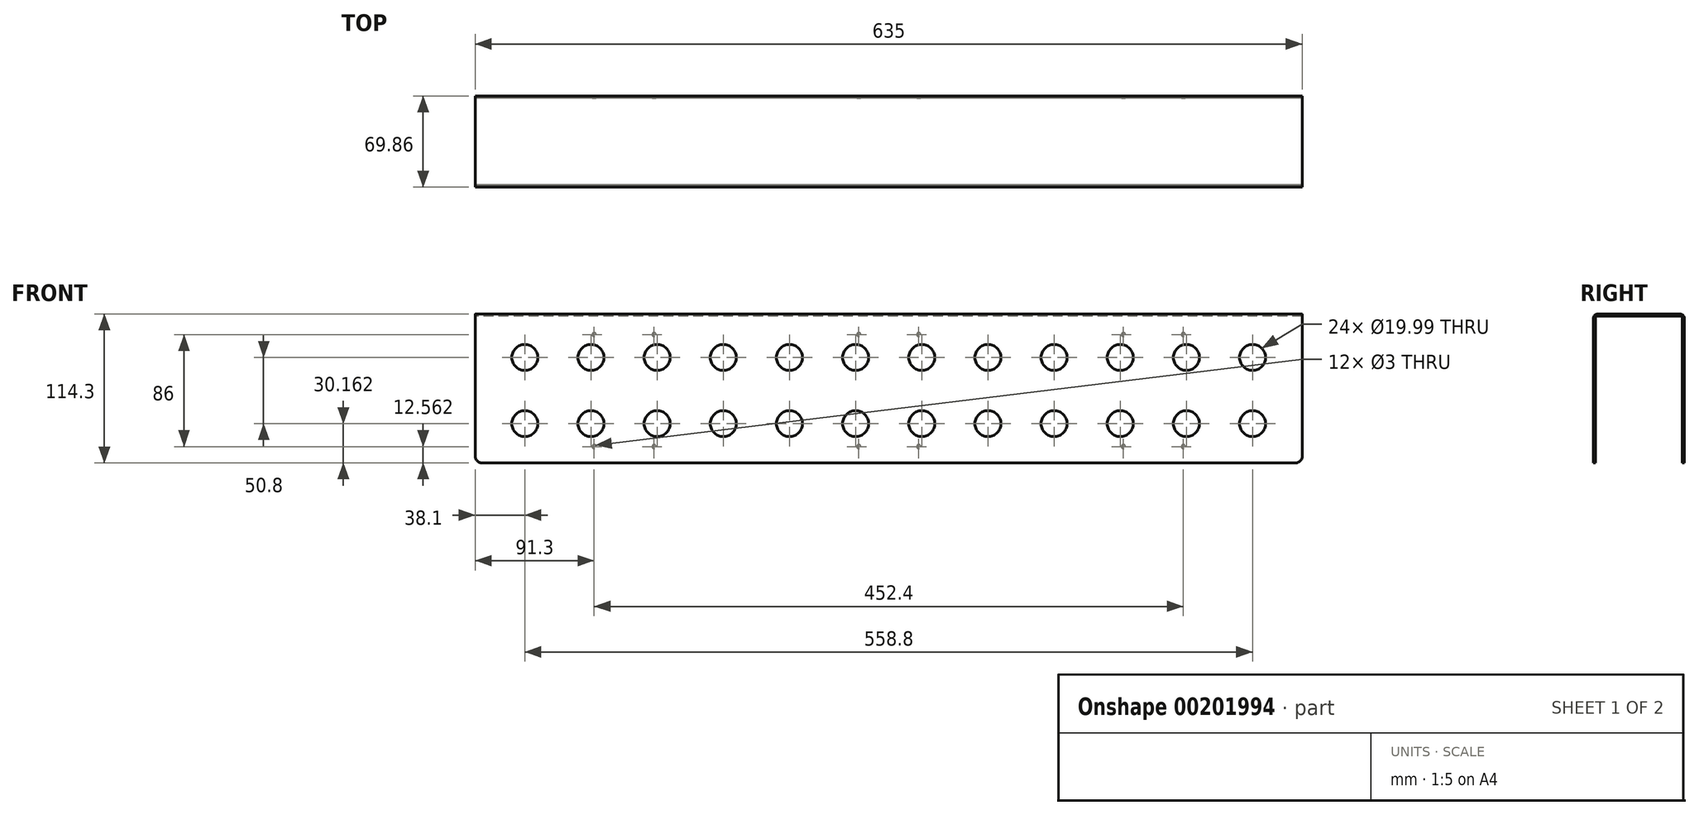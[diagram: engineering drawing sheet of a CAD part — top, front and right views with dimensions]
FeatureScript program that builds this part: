
annotation { "Feature Type Name" : "Feature", "Feature Type Description" : "" }
export const myFeature = defineFeature(function(context is Context, id is Id, definition is map)
    precondition{}
    {
        {
            var Q0;
            Q0=qCreatedBy(makeId("Right.planeOp"),FACE);
            var sketch = newSketch(context, id + "F0", { "sketchPlane" : qUnion([Q0])});
            skLineSegment(sketch, "E0", {"start": v(0, 0) * mm, "end": v(0, 85.98) * mm, "construction": true});
            skLineSegment(sketch, "E1", {"start": v(-31.75, 0) * mm, "end": v(31.75, 0) * mm});
            skLineSegment(sketch, "E2", {"start": v(34.93, -3.18) * mm, "end": v(34.93, -114.3) * mm});
            skLineSegment(sketch, "E3", {"start": v(-34.93, -3.18) * mm, "end": v(-34.92, -114.3) * mm});
            skPoint(sketch, "E4.visualSharp", {"position": v(-34.93, 0) * mm});
            skArc(sketch, "E4.filletArc", {"start": v(-31.75, 0) * mm, "mid": v(-34, -0.93) * mm, "end": v(-34.93, -3.18) * mm});
            skPoint(sketch, "E5.visualSharp", {"position": v(34.93, 0) * mm});
            skArc(sketch, "E5.filletArc", {"start": v(34.93, -3.18) * mm, "mid": v(34, -0.93) * mm, "end": v(31.75, 0) * mm});
            skLineSegment(sketch, "E6.0", {"start": v(-33.34, -3.17) * mm, "end": v(-33.34, -114.3) * mm});
            skLineSegment(sketch, "E6.1", {"start": v(-31.75, -1.59) * mm, "end": v(31.75, -1.59) * mm});
            skLineSegment(sketch, "E6.2", {"start": v(33.34, -3.17) * mm, "end": v(33.34, -114.3) * mm});
            skArc(sketch, "E7.filletArc", {"start": v(-31.75, -1.59) * mm, "mid": v(-32.87, -2.05) * mm, "end": v(-33.34, -3.17) * mm});
            skArc(sketch, "E8.filletArc", {"start": v(33.34, -3.17) * mm, "mid": v(32.87, -2.05) * mm, "end": v(31.75, -1.59) * mm});
            skLineSegment(sketch, "E9", {"start": v(-34.92, -114.3) * mm, "end": v(-33.34, -114.3) * mm});
            skLineSegment(sketch, "E10", {"start": v(33.34, -114.3) * mm, "end": v(34.93, -114.3) * mm});
            skSolve(sketch);
        }
        {
            var Q0;
            Q0 = qSketchRegion(id + "F0", true);
            extrude(context, id + "F1", {"entities" : qUnion([Q0]), "endBound" : BoundingType.SYMMETRIC, "depth" : 635 * mm});
        }
        {
            var Q0;
            Q0=makeQuery(id+"F1.opExtrude","SWEPT_FACE",FACE,{"disambiguationData":[OSD([sQuery(id+"F0.wireOp",EDGE,"E3")])]});
            var sketch = newSketch(context, id + "F2", { "sketchPlane" : qUnion([Q0])});
            skCircle(sketch, "E11", {"center": v(-279.4, -33.34) * mm, "radius": 10 * mm});
            skCircle(sketch, "E12.0.1.0", {"center": v(-279.4, -84.14) * mm, "radius": 10 * mm});
            skCircle(sketch, "E12.1.0.0", {"center": v(-228.6, -33.34) * mm, "radius": 10 * mm});
            skCircle(sketch, "E12.1.1.0", {"center": v(-228.6, -84.14) * mm, "radius": 10 * mm});
            skCircle(sketch, "E12.2.0.0", {"center": v(-177.8, -33.34) * mm, "radius": 10 * mm});
            skCircle(sketch, "E12.2.1.0", {"center": v(-177.8, -84.14) * mm, "radius": 10 * mm});
            skCircle(sketch, "E12.3.0.0", {"center": v(-127, -33.34) * mm, "radius": 10 * mm});
            skCircle(sketch, "E12.3.1.0", {"center": v(-127, -84.14) * mm, "radius": 10 * mm});
            skCircle(sketch, "E12.4.0.0", {"center": v(-76.2, -33.34) * mm, "radius": 10 * mm});
            skCircle(sketch, "E12.4.1.0", {"center": v(-76.2, -84.14) * mm, "radius": 10 * mm});
            skCircle(sketch, "E12.5.0.0", {"center": v(-25.4, -33.34) * mm, "radius": 10 * mm});
            skCircle(sketch, "E12.5.1.0", {"center": v(-25.4, -84.14) * mm, "radius": 10 * mm});
            skCircle(sketch, "E12.6.0.0", {"center": v(25.4, -33.34) * mm, "radius": 10 * mm});
            skCircle(sketch, "E12.6.1.0", {"center": v(25.4, -84.14) * mm, "radius": 10 * mm});
            skCircle(sketch, "E12.7.0.0", {"center": v(76.2, -33.34) * mm, "radius": 10 * mm});
            skCircle(sketch, "E12.7.1.0", {"center": v(76.2, -84.14) * mm, "radius": 10 * mm});
            skCircle(sketch, "E12.8.0.0", {"center": v(127, -33.34) * mm, "radius": 10 * mm});
            skCircle(sketch, "E12.8.1.0", {"center": v(127, -84.14) * mm, "radius": 10 * mm});
            skCircle(sketch, "E12.9.0.0", {"center": v(177.8, -33.34) * mm, "radius": 10 * mm});
            skCircle(sketch, "E12.9.1.0", {"center": v(177.8, -84.14) * mm, "radius": 10 * mm});
            skCircle(sketch, "E12.10.0.0", {"center": v(228.6, -33.34) * mm, "radius": 10 * mm});
            skCircle(sketch, "E12.10.1.0", {"center": v(228.6, -84.14) * mm, "radius": 10 * mm});
            skCircle(sketch, "E12.11.0.0", {"center": v(279.4, -33.34) * mm, "radius": 10 * mm});
            skCircle(sketch, "E12.11.1.0", {"center": v(279.4, -84.14) * mm, "radius": 10 * mm});
            skLineSegment(sketch, "E12.direction1", {"start": v(-279.4, -33.34) * mm, "end": v(-228.6, -33.34) * mm, "construction": true});
            skLineSegment(sketch, "E12.direction2", {"start": v(-279.4, -33.34) * mm, "end": v(-279.4, -84.14) * mm, "construction": true});
            skLineSegment(sketch, "E13", {"start": v(25.4, -84.14) * mm, "end": v(-25.4, -33.34) * mm, "construction": true});
            skLineSegment(sketch, "E14", {"start": v(0, -3.18) * mm, "end": v(0, -114.3) * mm, "construction": true});
            skPoint(sketch, "E15", {"position": v(0, -58.74) * mm});
            skSolve(sketch);
        }
        {
            var Q0;
            Q0 = qSketchRegion(id + "F2", true);
            extrude(context, id + "F3", {"entities" : qUnion([Q0]), "operationType" : NewBodyOperationType.REMOVE, "oppositeDirection" : true, "depth" : 25.4 * mm});
        }
        {
            var Q0;
            Q0=makeQuery(id+"F1.opExtrude","SWEPT_FACE",FACE,{"disambiguationData":[OSD([sQuery(id+"F0.wireOp",EDGE,"E2")])]});
            var sketch = newSketch(context, id + "F4", { "sketchPlane" : qUnion([Q0])});
            skCircle(sketch, "E16", {"center": v(-23, -15.74) * mm, "radius": 1.5 * mm});
            skCircle(sketch, "E17.0.1.0", {"center": v(-23, -101.74) * mm, "radius": 1.5 * mm});
            skCircle(sketch, "E17.1.0.0", {"center": v(23, -15.74) * mm, "radius": 1.5 * mm});
            skCircle(sketch, "E17.1.1.0", {"center": v(23, -101.74) * mm, "radius": 1.5 * mm});
            skLineSegment(sketch, "E17.direction1", {"start": v(-23, -15.74) * mm, "end": v(23, -15.74) * mm, "construction": true});
            skLineSegment(sketch, "E17.direction2", {"start": v(-23, -15.74) * mm, "end": v(-23, -101.74) * mm, "construction": true});
            skPoint(sketch, "E18", {"position": v(-23, -58.74) * mm});
            skPoint(sketch, "E19", {"position": v(-317.5, -58.74) * mm});
            skPoint(sketch, "E20", {"position": v(0, -15.74) * mm});
            skLineSegment(sketch, "E21", {"start": v(0, 0) * mm, "end": v(0, 50.3) * mm, "construction": true});
            skPoint(sketch, "E22.1.0.0", {"position": v(180.2, -58.74) * mm});
            skLineSegment(sketch, "E22.1.0.1", {"start": v(180.2, -15.74) * mm, "end": v(180.2, -101.74) * mm, "construction": true});
            skPoint(sketch, "E22.1.0.2", {"position": v(203.2, -15.74) * mm});
            skLineSegment(sketch, "E22.1.0.3", {"start": v(180.2, -15.74) * mm, "end": v(226.2, -15.74) * mm, "construction": true});
            skCircle(sketch, "E22.1.0.4", {"center": v(226.2, -101.74) * mm, "radius": 1.5 * mm});
            skCircle(sketch, "E22.1.0.5", {"center": v(180.2, -101.74) * mm, "radius": 1.5 * mm});
            skCircle(sketch, "E22.1.0.6", {"center": v(226.2, -15.74) * mm, "radius": 1.5 * mm});
            skCircle(sketch, "E22.1.0.7", {"center": v(180.2, -15.74) * mm, "radius": 1.5 * mm});
            skLineSegment(sketch, "E22.direction1", {"start": v(-23, -101.74) * mm, "end": v(180.2, -101.74) * mm, "construction": true});
            skCircle(sketch, "E23.MirrorC", {"center": v(-226.2, -15.74) * mm, "radius": 1.5 * mm});
            skCircle(sketch, "E24.MirrorC", {"center": v(-180.2, -15.74) * mm, "radius": 1.5 * mm});
            skCircle(sketch, "E25.MirrorC", {"center": v(-180.2, -101.74) * mm, "radius": 1.5 * mm});
            skCircle(sketch, "E26.MirrorC", {"center": v(-226.2, -101.74) * mm, "radius": 1.5 * mm});
            skSolve(sketch);
        }
        {
            var Q0;
            Q0 = qSketchRegion(id + "F4", true);
            extrude(context, id + "F5", {"entities" : qUnion([Q0]), "operationType" : NewBodyOperationType.REMOVE, "oppositeDirection" : true, "depth" : 25.4 * mm});
        }
        {
            var Q0;
            Q0=makeQuery(id+"F1.opExtrude","CAP_EDGE",EDGE,{"disambiguationData":[OSD([sQuery(id+"F0.wireOp",EDGE,"E9")])],"isStart":true});
            var Q1;
            Q1=makeQuery(id+"F1.opExtrude","CAP_EDGE",EDGE,{"disambiguationData":[OSD([sQuery(id+"F0.wireOp",EDGE,"E10")])],"isStart":true});
            var Q2;
            Q2=makeQuery(id+"F1.opExtrude","CAP_EDGE",EDGE,{"disambiguationData":[OSD([sQuery(id+"F0.wireOp",EDGE,"E9")])],"isStart":false});
            var Q3;
            Q3=makeQuery(id+"F1.opExtrude","CAP_EDGE",EDGE,{"disambiguationData":[OSD([sQuery(id+"F0.wireOp",EDGE,"E10")])],"isStart":false});
            fillet(context, id + "F6", {"entities" : qUnion([Q0, Q1, Q2, Q3]), "radius" : 5.08 * mm, "tangentPropagation" : true, "allowEdgeOverflow" : false});
        }
    });
